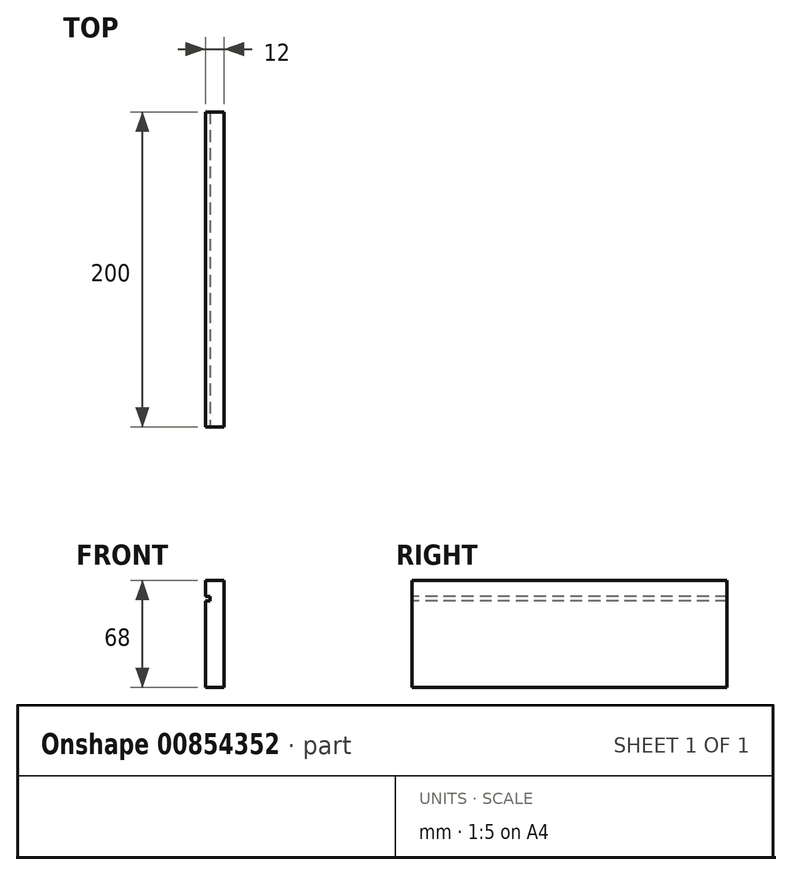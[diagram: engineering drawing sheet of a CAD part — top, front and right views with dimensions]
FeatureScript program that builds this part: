
annotation { "Feature Type Name" : "Feature", "Feature Type Description" : "" }
export const myFeature = defineFeature(function(context is Context, id is Id, definition is map)
    precondition{}
    {
        {
            var Q0;
            Q0=qCreatedBy(makeId("Right.planeOp"),FACE);
            var sketch = newSketch(context, id + "F0", { "sketchPlane" : qUnion([Q0])});
            skLineSegment(sketch, "E0.bottom", {"start": v(-100, 34) * mm, "end": v(100, 34) * mm});
            skLineSegment(sketch, "E0.top", {"start": v(-100, -34) * mm, "end": v(100, -34) * mm});
            skLineSegment(sketch, "E0.left", {"start": v(-100, 34) * mm, "end": v(-100, -34) * mm});
            skLineSegment(sketch, "E0.right", {"start": v(100, 34) * mm, "end": v(100, -34) * mm});
            skPoint(sketch, "E0.middle", {"position": v(0, 0) * mm});
            skSolve(sketch);
        }
        {
            var Q0;
            Q0 = qSketchRegion(id + "F0", true);
            extrude(context, id + "F1", {"entities" : qUnion([Q0]), "depth" : 12 * mm, "offsetDistance" : 25.4 * mm});
        }
        {
            var Q0;
            Q0=makeQuery(id+"F1.opExtrude","SWEPT_FACE",FACE,{"disambiguationData":[OSD([sQuery(id+"F0.wireOp",EDGE,"E0.left")])]});
            var sketch = newSketch(context, id + "F2", { "sketchPlane" : qUnion([Q0])});
            skLineSegment(sketch, "E1.bottom", {"start": v(0, 24) * mm, "end": v(3, 24) * mm});
            skLineSegment(sketch, "E1.top", {"start": v(0, 21) * mm, "end": v(3, 21) * mm});
            skLineSegment(sketch, "E1.left", {"start": v(0, 24) * mm, "end": v(0, 21) * mm});
            skLineSegment(sketch, "E1.right", {"start": v(3, 24) * mm, "end": v(3, 21) * mm});
            skSolve(sketch);
        }
        {
            var Q0;
            Q0 = qSketchRegion(id + "F2", true);
            extrude(context, id + "F3", {"entities" : qUnion([Q0]), "operationType" : NewBodyOperationType.REMOVE, "oppositeDirection" : true, "depth" : 32123 * mm, "offsetDistance" : 25.4 * mm});
        }
        {
            var Q0;
            Q0=makeQuery(id+"F1.opExtrude","SWEPT_FACE",FACE,{"disambiguationData":[OSD([sQuery(id+"F0.wireOp",EDGE,"E0.left")])]});
            var sketch = newSketch(context, id + "F4", { "sketchPlane" : qUnion([Q0])});
            skLineSegment(sketch, "E2.bottom", {"start": v(3, 21) * mm, "end": v(0, 21) * mm});
            skLineSegment(sketch, "E2.top", {"start": v(3, 24) * mm, "end": v(0, 24) * mm});
            skLineSegment(sketch, "E2.left", {"start": v(3, 21) * mm, "end": v(3, 24) * mm});
            skLineSegment(sketch, "E2.right", {"start": v(0, 21) * mm, "end": v(0, 24) * mm});
            skSolve(sketch);
        }
        {
            var Q0;
            Q0=makeQuery(id+"F4.imprint","IMPRINT",FACE,{"disambiguationData":[TD([[makeQuery(id+"F4.imprint","IMPRINT",EDGE,{"derivedFrom":sQuery(id+"F4.wireOp",EDGE,"E2.bottom")}),1.0]])]});
            extrude(context, id + "F5", {"entities" : qUnion([Q0]), "operationType" : NewBodyOperationType.REMOVE, "oppositeDirection" : true, "depth" : 20 * mm, "offsetDistance" : 25.4 * mm});
        }
    });
